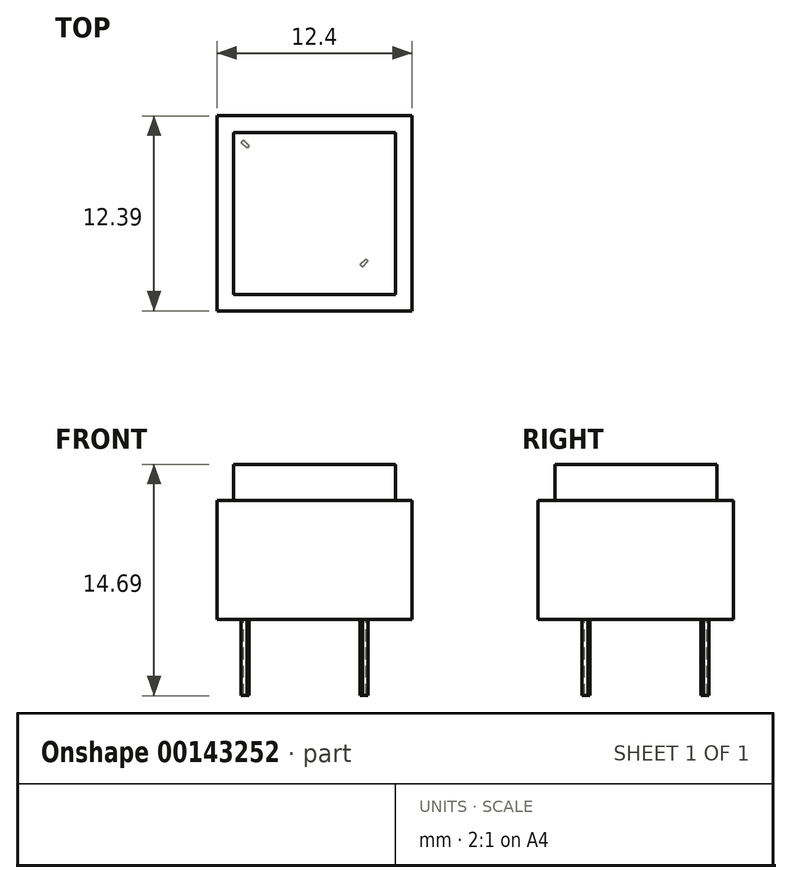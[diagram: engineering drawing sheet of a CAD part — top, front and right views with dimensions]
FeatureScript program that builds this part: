
annotation { "Feature Type Name" : "Feature", "Feature Type Description" : "" }
export const myFeature = defineFeature(function(context is Context, id is Id, definition is map)
    precondition{}
    {
        {
            var Q0;
            Q0=qCreatedBy(makeId("Top.planeOp"),FACE);
            var sketch = newSketch(context, id + "F0", { "sketchPlane" : qUnion([Q0])});
            skLineSegment(sketch, "E0.bottom", {"start": v(-5.95, 4.28) * mm, "end": v(6.45, 4.28) * mm});
            skLineSegment(sketch, "E0.top", {"start": v(-5.95, -8.11) * mm, "end": v(6.45, -8.11) * mm});
            skLineSegment(sketch, "E0.left", {"start": v(-5.95, 4.28) * mm, "end": v(-5.95, -8.11) * mm});
            skLineSegment(sketch, "E0.right", {"start": v(6.45, 4.28) * mm, "end": v(6.45, -8.11) * mm});
            skLineSegment(sketch, "E1.bottom", {"start": v(5.4, -7.06) * mm, "end": v(-4.9, -7.06) * mm});
            skLineSegment(sketch, "E1.top", {"start": v(5.4, 3.23) * mm, "end": v(-4.9, 3.23) * mm});
            skLineSegment(sketch, "E1.left", {"start": v(5.4, -7.06) * mm, "end": v(5.4, 3.23) * mm});
            skLineSegment(sketch, "E1.right", {"start": v(-4.9, -7.06) * mm, "end": v(-4.9, 3.23) * mm});
            skPoint(sketch, "E1.middle", {"position": v(0.25, -1.92) * mm});
            skPoint(sketch, "E1.middle.positionSnap0", {"position": v(0.25, -8.11) * mm});
            skPoint(sketch, "E1.middle.positionSnap1", {"position": v(-5.95, -1.92) * mm});
            skPoint(sketch, "E1.centerSnap0", {"position": v(0.25, -8.11) * mm});
            skPoint(sketch, "E1.centerSnap1", {"position": v(-5.95, -1.92) * mm});
            skSolve(sketch);
        }
        {
            var Q0;
            Q0=makeQuery(id+"F0.imprint","IMPRINT",FACE,{"disambiguationData":[TD([[makeQuery(id+"F0.imprint","IMPRINT",EDGE,{"derivedFrom":sQuery(id+"F0.wireOp",EDGE,"E0.bottom")}),-1.0]])]});
            var Q1;
            Q1=makeQuery(id+"F0.imprint","IMPRINT",FACE,{"disambiguationData":[TD([[makeQuery(id+"F0.imprint","IMPRINT",EDGE,{"derivedFrom":sQuery(id+"F0.wireOp",EDGE,"E1.bottom")}),-1.0]])]});
            extrude(context, id + "F1", {"entities" : qUnion([Q0, Q1]), "oppositeDirection" : true, "depth" : 7.57 * mm});
        }
        {
            var Q0;
            Q0=makeQuery(id+"F0.imprint","IMPRINT",FACE,{"disambiguationData":[TD([[makeQuery(id+"F0.imprint","IMPRINT",EDGE,{"derivedFrom":sQuery(id+"F0.wireOp",EDGE,"E1.bottom")}),-1.0]])]});
            extrude(context, id + "F2", {"entities" : qUnion([Q0]), "operationType" : NewBodyOperationType.ADD, "depth" : 2.3 * mm});
        }
        {
            var Q0;
            Q0=makeQuery(id+"F1.opExtrude","CAP_FACE",FACE,{"disambiguationData":[OSD([sQuery(id+"F0.wireOp",EDGE,"E0.bottom"),sQuery(id+"F0.wireOp",EDGE,"E0.top"),sQuery(id+"F0.wireOp",EDGE,"E0.left"),sQuery(id+"F0.wireOp",EDGE,"E0.right")])],"isStart":false});
            var sketch = newSketch(context, id + "F3", { "sketchPlane" : qUnion([Q0])});
            skLineSegment(sketch, "E2.0", {"start": v(-5.95, -4.28) * mm, "end": v(-5.95, 8.11) * mm});
            skLineSegment(sketch, "E3.0", {"start": v(-5.95, -4.28) * mm, "end": v(6.45, -4.28) * mm});
            skLineSegment(sketch, "E4.0", {"start": v(6.45, -4.28) * mm, "end": v(6.45, 8.11) * mm});
            skLineSegment(sketch, "E5.0", {"start": v(-5.95, 8.11) * mm, "end": v(6.45, 8.11) * mm});
            skLineSegment(sketch, "E6", {"start": v(-2.4, -4.28) * mm, "end": v(-5.95, -0.73) * mm});
            skLineSegment(sketch, "E7", {"start": v(-5.95, -4.28) * mm, "end": v(-3.74, -2.08) * mm});
            skLineSegment(sketch, "E8", {"start": v(-4.33, -2.67) * mm, "end": v(-4.4, -2.6) * mm});
            skLineSegment(sketch, "E9", {"start": v(-4.4, -2.6) * mm, "end": v(-4.05, -2.24) * mm});
            skLineSegment(sketch, "E10", {"start": v(-4.05, -2.24) * mm, "end": v(-3.98, -2.3) * mm});
            skLineSegment(sketch, "E11.MirrorCS", {"start": v(-4.33, -2.67) * mm, "end": v(-4.26, -2.74) * mm});
            skLineSegment(sketch, "E12.MirrorCS", {"start": v(-4.26, -2.74) * mm, "end": v(-3.9, -2.38) * mm});
            skLineSegment(sketch, "E13.MirrorCS", {"start": v(-3.9, -2.38) * mm, "end": v(-3.98, -2.3) * mm});
            skLineSegment(sketch, "E14", {"start": v(6.45, 2.16) * mm, "end": v(0.5, 8.11) * mm});
            skLineSegment(sketch, "E15", {"start": v(3.47, 5.14) * mm, "end": v(3.32, 5) * mm});
            skLineSegment(sketch, "E16", {"start": v(3.32, 5) * mm, "end": v(3.5, 4.81) * mm});
            skLineSegment(sketch, "E17", {"start": v(3.32, 5) * mm, "end": v(3.14, 5.17) * mm});
            skLineSegment(sketch, "E18", {"start": v(3.14, 5.17) * mm, "end": v(3.29, 5.32) * mm});
            skLineSegment(sketch, "E19", {"start": v(3.5, 4.81) * mm, "end": v(3.65, 4.96) * mm});
            skSolve(sketch);
        }
        {
            var Q0;
            {var subQ5=sQuery(id+"F3.wireOp",EDGE,"E8");Q0=makeQuery(id+"F3.imprint","IMPRINT",FACE,{"disambiguationData":[TD([[makeQuery(id+"F3.imprint","IMPRINT",EDGE,{"derivedFrom":subQ5}),-1.0]])]});}
            var Q1;
            {var subQ5=sQuery(id+"F3.wireOp",EDGE,"E11.MirrorCS");Q1=makeQuery(id+"F3.imprint","IMPRINT",FACE,{"disambiguationData":[TD([[makeQuery(id+"F3.imprint","IMPRINT",EDGE,{"derivedFrom":subQ5}),1.0]])]});}
            var Q2;
            {var subQ5=sQuery(id+"F3.wireOp",EDGE,"E13.MirrorCS");Q2=makeQuery(id+"F3.imprint","IMPRINT",FACE,{"disambiguationData":[TD([[makeQuery(id+"F3.imprint","IMPRINT",EDGE,{"derivedFrom":subQ5}),1.0]])]});}
            var Q3;
            {var subQ5=sQuery(id+"F3.wireOp",EDGE,"E10");Q3=makeQuery(id+"F3.imprint","IMPRINT",FACE,{"disambiguationData":[TD([[makeQuery(id+"F3.imprint","IMPRINT",EDGE,{"derivedFrom":subQ5}),-1.0]])]});}
            var Q4;
            {var subQ0=sQuery(id+"F3.wireOp",EDGE,"E15");Q4=makeQuery(id+"F3.imprint","IMPRINT",FACE,{"disambiguationData":[TD([[makeQuery(id+"F3.imprint","IMPRINT",EDGE,{"derivedFrom":subQ0}),-1.0]])]});}
            var Q5;
            {var subQ0=sQuery(id+"F3.wireOp",EDGE,"E15");Q5=makeQuery(id+"F3.imprint","IMPRINT",FACE,{"disambiguationData":[TD([[makeQuery(id+"F3.imprint","IMPRINT",EDGE,{"derivedFrom":subQ0}),1.0]])]});}
            extrude(context, id + "F4", {"entities" : qUnion([Q0, Q1, Q2, Q3, Q4, Q5]), "operationType" : NewBodyOperationType.ADD, "depth" : 4.83 * mm});
        }
    });
